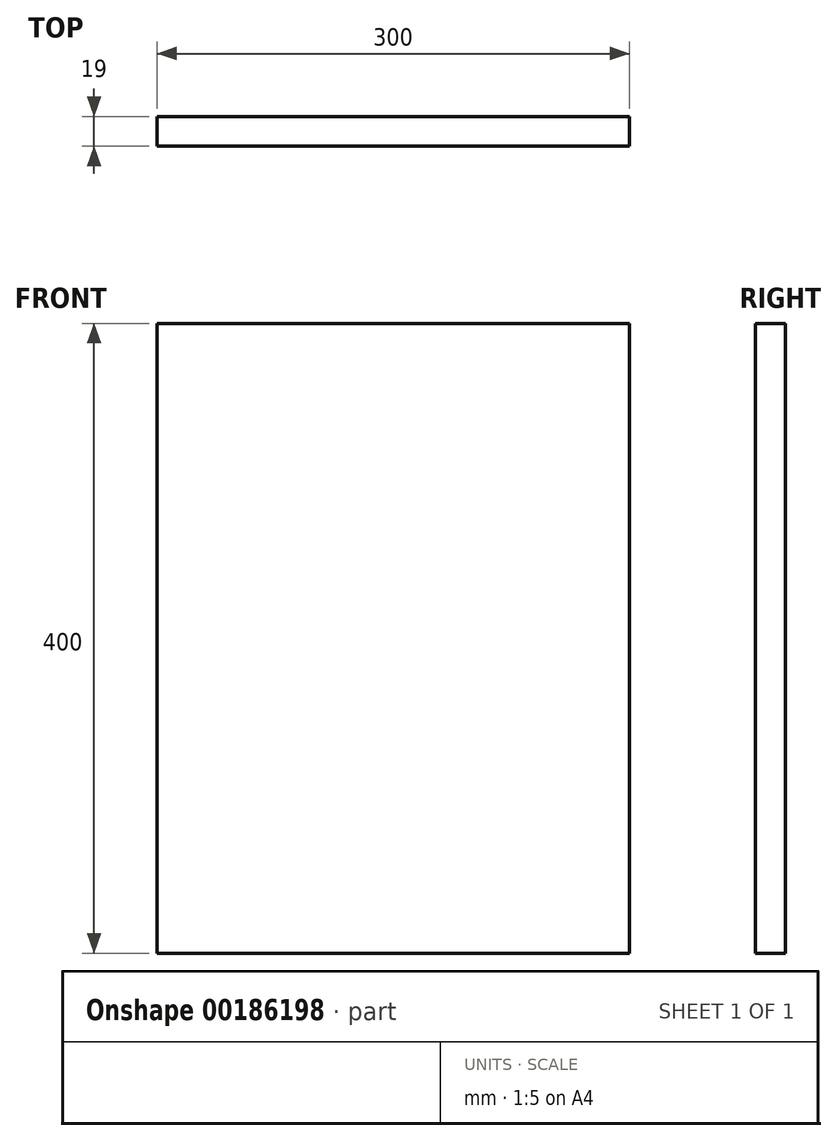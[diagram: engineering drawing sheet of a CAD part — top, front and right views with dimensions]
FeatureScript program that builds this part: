
annotation { "Feature Type Name" : "Feature", "Feature Type Description" : "" }
export const myFeature = defineFeature(function(context is Context, id is Id, definition is map)
    precondition{}
    {
        {
            var Q0;
            Q0=qCreatedBy(makeId("Front.planeOp"),FACE);
            var sketch = newSketch(context, id + "F0", { "sketchPlane" : qUnion([Q0])});
            skLineSegment(sketch, "E0.bottom", {"start": v(-208.43, 347.98) * mm, "end": v(91.57, 347.98) * mm});
            skLineSegment(sketch, "E0.top", {"start": v(-208.43, -52.02) * mm, "end": v(91.57, -52.02) * mm});
            skLineSegment(sketch, "E0.left", {"start": v(-208.43, 347.98) * mm, "end": v(-208.43, -52.02) * mm});
            skLineSegment(sketch, "E0.right", {"start": v(91.57, 347.98) * mm, "end": v(91.57, -52.02) * mm});
            skSolve(sketch);
        }
        {
            var Q0;
            Q0=makeQuery(id+"F0.imprint","IMPRINT",FACE,{"disambiguationData":[TD([[makeQuery(id+"F0.imprint","IMPRINT",EDGE,{"derivedFrom":sQuery(id+"F0.wireOp",EDGE,"E0.bottom")}),-1.0]])]});
            extrude(context, id + "F1", {"entities" : qUnion([Q0]), "depth" : 19 * mm});
        }
    });
